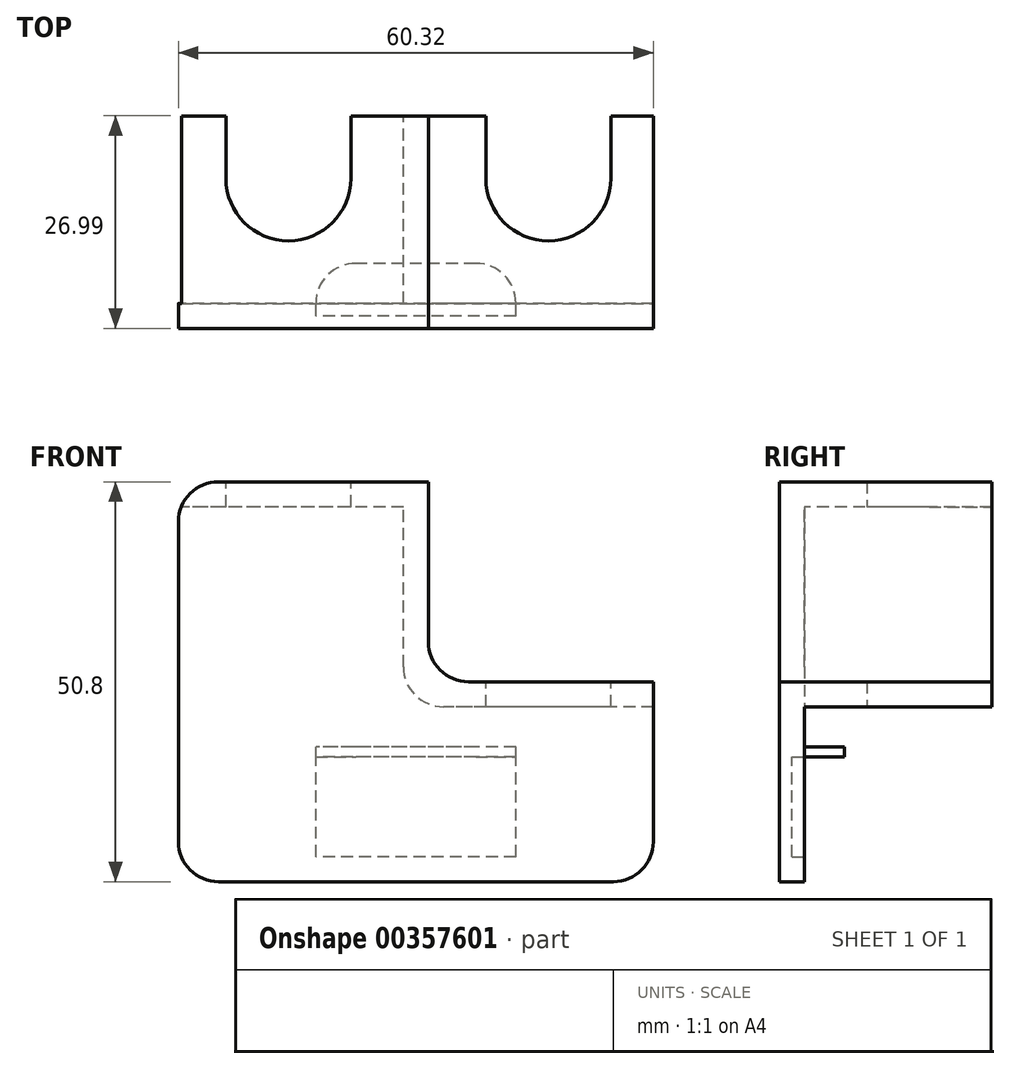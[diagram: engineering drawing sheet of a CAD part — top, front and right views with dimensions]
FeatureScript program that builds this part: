
annotation { "Feature Type Name" : "Feature", "Feature Type Description" : "" }
export const myFeature = defineFeature(function(context is Context, id is Id, definition is map)
    precondition{}
    {
        {
            var Q0;
            Q0=qCreatedBy(makeId("Front.planeOp"),FACE);
            var sketch = newSketch(context, id + "F0", { "sketchPlane" : qUnion([Q0])});
            skLineSegment(sketch, "E0", {"start": v(-28.58, 25.4) * mm, "end": v(0, 25.4) * mm});
            skLineSegment(sketch, "E1", {"start": v(0, 25.4) * mm, "end": v(0, 0) * mm});
            skLineSegment(sketch, "E2", {"start": v(0, 0) * mm, "end": v(25.4, 0) * mm});
            skLineSegment(sketch, "E3", {"start": v(25.4, 0) * mm, "end": v(25.4, -3.18) * mm});
            skLineSegment(sketch, "E4", {"start": v(25.4, -3.18) * mm, "end": v(-3.18, -3.18) * mm});
            skLineSegment(sketch, "E5", {"start": v(-3.18, -3.18) * mm, "end": v(-3.18, 22.22) * mm});
            skLineSegment(sketch, "E6", {"start": v(-3.18, 22.22) * mm, "end": v(-28.58, 22.22) * mm});
            skLineSegment(sketch, "E7", {"start": v(-28.58, 22.22) * mm, "end": v(-28.58, 25.4) * mm});
            skSolve(sketch);
        }
        {
            var Q0;
            Q0=makeQuery(id+"F0.imprint","IMPRINT",FACE,{"disambiguationData":[TD([[makeQuery(id+"F0.imprint","IMPRINT",EDGE,{"derivedFrom":sQuery(id+"F0.wireOp",EDGE,"E0")}),-1.0]])]});
            extrude(context, id + "F1", {"entities" : qUnion([Q0]), "offsetDistance" : 25.4 * mm, "depth" : 28.57 * mm});
        }
        {
            var Q0;
            Q0=makeQuery(id+"F1.opExtrude","SWEPT_FACE",FACE,{"disambiguationData":[OSD([sQuery(id+"F0.wireOp",EDGE,"E4")])]});
            var sketch = newSketch(context, id + "F2", { "sketchPlane" : qUnion([Q0])});
            skCircle(sketch, "E8", {"center": v(-17.78, 12.7) * mm, "radius": 7.94 * mm});
            skCircle(sketch, "E9", {"center": v(15.24, 12.7) * mm, "radius": 7.94 * mm});
            skSolve(sketch);
        }
        {
            var Q0;
            Q0=makeQuery(id+"F2.imprint","IMPRINT",FACE,{"disambiguationData":[TD([[makeQuery(id+"F2.imprint","IMPRINT",EDGE,{"derivedFrom":sQuery(id+"F2.wireOp",EDGE,"E8")}),1.0]])]});
            var Q1;
            Q1=makeQuery(id+"F2.imprint","IMPRINT",FACE,{"disambiguationData":[TD([[makeQuery(id+"F2.imprint","IMPRINT",EDGE,{"derivedFrom":sQuery(id+"F2.wireOp",EDGE,"E9")}),1.0]])]});
            var Q2;
            Q2=makeQuery(id+"F2.imprint","IMPRINT",FACE,{"disambiguationData":[TD([[makeQuery(id+"F2.imprint","IMPRINT",EDGE,{"derivedFrom":sQuery(id+"F2.wireOp",EDGE,"E9")}),1.0]])]});
            extrude(context, id + "F3", {"entities" : qUnion([Q0, Q1, Q2]), "operationType" : NewBodyOperationType.REMOVE, "oppositeDirection" : true, "depth" : 50.8 * mm});
        }
        {
            var Q0;
            Q0=makeQuery(id+"F1.opExtrude","SWEPT_FACE",FACE,{"disambiguationData":[OSD([sQuery(id+"F0.wireOp",EDGE,"E0")])]});
            var sketch = newSketch(context, id + "F4", { "sketchPlane" : qUnion([Q0])});
            skLineSegment(sketch, "E10.bottom", {"start": v(-28.58, 0) * mm, "end": v(25.4, 0) * mm});
            skLineSegment(sketch, "E10.top", {"start": v(-28.58, -28.58) * mm, "end": v(25.4, -28.58) * mm});
            skLineSegment(sketch, "E10.left", {"start": v(-28.58, 0) * mm, "end": v(-28.58, -28.58) * mm});
            skLineSegment(sketch, "E10.right", {"start": v(25.4, 0) * mm, "end": v(25.4, -28.58) * mm});
            skLineSegment(sketch, "E11.0", {"start": v(-31.75, 3.18) * mm, "end": v(28.57, 3.18) * mm});
            skLineSegment(sketch, "E12.0", {"start": v(-31.75, 3.18) * mm, "end": v(-31.75, -31.75) * mm});
            skLineSegment(sketch, "E12.1", {"start": v(-31.75, -31.75) * mm, "end": v(28.57, -31.75) * mm});
            skLineSegment(sketch, "E12.2", {"start": v(28.57, 3.17) * mm, "end": v(28.57, -31.75) * mm});
            skSolve(sketch);
        }
        {
            var Q0;
            {var subQ4=sQuery(id+"F4.wireOp",EDGE,"E10.left");Q0=makeQuery(id+"F4.imprint","IMPRINT",FACE,{"disambiguationData":[TD([[makeQuery(id+"F4.imprint","IMPRINT",EDGE,{"derivedFrom":subQ4}),1.0]])]});}
            extrude(context, id + "F5", {"entities" : qUnion([Q0]), "operationType" : NewBodyOperationType.ADD, "oppositeDirection" : true, "depth" : 50.8 * mm});
        }
        {
            var Q0;
            {var subQ2=sQuery(id+"F4.wireOp",EDGE,"E10.top");Q0=makeQuery(id+"F5.boolean.opBoolean","SPLIT",FACE,{"disambiguationData":[TD([makeQuery(id+"F1.opExtrude","SWEPT_FACE",FACE,{"disambiguationData":[OSD([sQuery(id+"F0.wireOp",EDGE,"E4")])]})])],"derivedFrom":makeQuery(id+"F5.opExtrude","SWEPT_FACE",FACE,{"disambiguationData":[OSD([subQ2])]})});}
            var sketch = newSketch(context, id + "F6", { "sketchPlane" : qUnion([Q0])});
            skLineSegment(sketch, "E13.bottom", {"start": v(-11.11, -22.23) * mm, "end": v(14.29, -22.23) * mm});
            skLineSegment(sketch, "E13.top", {"start": v(-11.11, -9.53) * mm, "end": v(14.29, -9.53) * mm});
            skLineSegment(sketch, "E13.left", {"start": v(-11.11, -22.23) * mm, "end": v(-11.11, -9.53) * mm});
            skLineSegment(sketch, "E13.right", {"start": v(14.29, -22.23) * mm, "end": v(14.29, -9.53) * mm});
            skPoint(sketch, "E13.middle", {"position": v(1.59, -15.88) * mm});
            skSolve(sketch);
        }
        {
            var Q0;
            Q0=makeQuery(id+"F6.imprint","IMPRINT",FACE,{"disambiguationData":[TD([[makeQuery(id+"F6.imprint","IMPRINT",EDGE,{"derivedFrom":sQuery(id+"F6.wireOp",EDGE,"E13.bottom")}),1.0]])]});
            extrude(context, id + "F7", {"entities" : qUnion([Q0]), "operationType" : NewBodyOperationType.REMOVE, "oppositeDirection" : true, "depth" : 1.59 * mm});
        }
        {
            var Q0;
            Q0=makeQuery(id+"F5.boolean.opBoolean","MERGE",FACE,{"derivedFrom":[makeQuery(id+"F1.opExtrude","SWEPT_FACE",FACE,{"disambiguationData":[OSD([sQuery(id+"F0.wireOp",EDGE,"E0")])]}),makeQuery(id+"F5.opExtrude","CAP_FACE",FACE,{"disambiguationData":[OSD([sQuery(id+"F4.wireOp",EDGE,"E10.bottom"),sQuery(id+"F4.wireOp",EDGE,"E10.top"),sQuery(id+"F4.wireOp",EDGE,"E10.left"),sQuery(id+"F4.wireOp",EDGE,"E10.right"),sQuery(id+"F4.wireOp",EDGE,"E11.0"),sQuery(id+"F4.wireOp",EDGE,"E12.0"),sQuery(id+"F4.wireOp",EDGE,"E12.1"),sQuery(id+"F4.wireOp",EDGE,"E12.2")])],"isStart":true})]});
            var sketch = newSketch(context, id + "F8", { "sketchPlane" : qUnion([Q0])});
            skLineSegment(sketch, "E14.bottom", {"start": v(-31.75, -4.76) * mm, "end": v(28.57, -4.76) * mm});
            skLineSegment(sketch, "E14.top", {"start": v(-31.75, 3.18) * mm, "end": v(28.57, 3.18) * mm});
            skLineSegment(sketch, "E14.left", {"start": v(-31.75, -4.76) * mm, "end": v(-31.75, 3.18) * mm});
            skLineSegment(sketch, "E14.right", {"start": v(28.57, -4.76) * mm, "end": v(28.57, 3.18) * mm});
            skLineSegment(sketch, "E15", {"start": v(-25.72, -4.76) * mm, "end": v(-25.72, -12.7) * mm});
            skLineSegment(sketch, "E16", {"start": v(-9.84, -12.7) * mm, "end": v(-9.84, -4.76) * mm});
            skLineSegment(sketch, "E17", {"start": v(7.3, -4.76) * mm, "end": v(7.3, -12.7) * mm});
            skLineSegment(sketch, "E18", {"start": v(23.18, -4.76) * mm, "end": v(23.18, -12.7) * mm});
            skCircle(sketch, "E19", {"center": v(15.24, -12.7) * mm, "radius": 7.94 * mm});
            skSolve(sketch);
        }
        {
            var Q0;
            {var subQ1=sQuery(id+"F4.wireOp",EDGE,"E12.0");var subQ2=sQuery(id+"F4.wireOp",EDGE,"E11.0");var subQ3=makeQuery(id+"Fs04usrGWM9eHkK_1.opFillet","BLEND_EDGE",EDGE,{"blendedFrom":[makeQuery(id+"F5.opExtrude","SWEPT_EDGE",EDGE,{"disambiguationData":[OSD([subQ2,subQ1])]}),makeQuery(id+"F5.boolean.opBoolean","MERGE",FACE,{"derivedFrom":[makeQuery(id+"F1.opExtrude","SWEPT_FACE",FACE,{"disambiguationData":[OSD([sQuery(id+"F0.wireOp",EDGE,"E0")])]}),makeQuery(id+"F5.opExtrude","CAP_FACE",FACE,{"disambiguationData":[OSD([sQuery(id+"F4.wireOp",EDGE,"E10.bottom"),sQuery(id+"F4.wireOp",EDGE,"E10.top"),sQuery(id+"F4.wireOp",EDGE,"E10.left"),sQuery(id+"F4.wireOp",EDGE,"E10.right"),subQ2,subQ1,sQuery(id+"F4.wireOp",EDGE,"E12.1"),sQuery(id+"F4.wireOp",EDGE,"E12.2")])],"isStart":true})]})],"blendedInto":[makeQuery(id+"F5.boolean.opBoolean","MERGE",FACE,{"derivedFrom":[makeQuery(id+"F1.opExtrude","SWEPT_FACE",FACE,{"disambiguationData":[OSD([sQuery(id+"F0.wireOp",EDGE,"E0")])]}),makeQuery(id+"F5.opExtrude","CAP_FACE",FACE,{"disambiguationData":[OSD([sQuery(id+"F4.wireOp",EDGE,"E10.bottom"),sQuery(id+"F4.wireOp",EDGE,"E10.top"),sQuery(id+"F4.wireOp",EDGE,"E10.left"),sQuery(id+"F4.wireOp",EDGE,"E10.right"),subQ2,subQ1,sQuery(id+"F4.wireOp",EDGE,"E12.1"),sQuery(id+"F4.wireOp",EDGE,"E12.2")])],"isStart":true})]})]});Q0=makeQuery(id+"F8.imprint","IMPRINT",FACE,{"disambiguationData":[TD([[makeQuery(id+"F8.imprint","IMPRINT",EDGE,{"derivedFrom":subQ3}),-1.0]])]});}
            var Q1;
            {var subQ1=sQuery(id+"F4.wireOp",EDGE,"E12.2");var subQ2=sQuery(id+"F4.wireOp",EDGE,"E11.0");var subQ3=makeQuery(id+"Fs04usrGWM9eHkK_1.opFillet","BLEND_EDGE",EDGE,{"blendedFrom":[makeQuery(id+"F5.opExtrude","SWEPT_EDGE",EDGE,{"disambiguationData":[OSD([subQ2,subQ1])]}),makeQuery(id+"F5.boolean.opBoolean","MERGE",FACE,{"derivedFrom":[makeQuery(id+"F1.opExtrude","SWEPT_FACE",FACE,{"disambiguationData":[OSD([sQuery(id+"F0.wireOp",EDGE,"E0")])]}),makeQuery(id+"F5.opExtrude","CAP_FACE",FACE,{"disambiguationData":[OSD([sQuery(id+"F4.wireOp",EDGE,"E10.bottom"),sQuery(id+"F4.wireOp",EDGE,"E10.top"),sQuery(id+"F4.wireOp",EDGE,"E10.left"),sQuery(id+"F4.wireOp",EDGE,"E10.right"),subQ2,sQuery(id+"F4.wireOp",EDGE,"E12.0"),sQuery(id+"F4.wireOp",EDGE,"E12.1"),subQ1])],"isStart":true})]})],"blendedInto":[makeQuery(id+"F5.boolean.opBoolean","MERGE",FACE,{"derivedFrom":[makeQuery(id+"F1.opExtrude","SWEPT_FACE",FACE,{"disambiguationData":[OSD([sQuery(id+"F0.wireOp",EDGE,"E0")])]}),makeQuery(id+"F5.opExtrude","CAP_FACE",FACE,{"disambiguationData":[OSD([sQuery(id+"F4.wireOp",EDGE,"E10.bottom"),sQuery(id+"F4.wireOp",EDGE,"E10.top"),sQuery(id+"F4.wireOp",EDGE,"E10.left"),sQuery(id+"F4.wireOp",EDGE,"E10.right"),subQ2,sQuery(id+"F4.wireOp",EDGE,"E12.0"),sQuery(id+"F4.wireOp",EDGE,"E12.1"),subQ1])],"isStart":true})]})]});Q1=makeQuery(id+"F8.imprint","IMPRINT",FACE,{"disambiguationData":[TD([[makeQuery(id+"F8.imprint","IMPRINT",EDGE,{"derivedFrom":subQ3}),-1.0]])]});}
            var Q2;
            {var subQ0=sQuery(id+"F8.wireOp",EDGE,"E17");Q2=makeQuery(id+"F8.imprint","IMPRINT",FACE,{"disambiguationData":[TD([[makeQuery(id+"F8.imprint","IMPRINT",EDGE,{"derivedFrom":subQ0}),1.0]])]});}
            var Q3;
            {var subQ0=sQuery(id+"F8.wireOp",EDGE,"E18");Q3=makeQuery(id+"F8.imprint","IMPRINT",FACE,{"disambiguationData":[TD([[makeQuery(id+"F8.imprint","IMPRINT",EDGE,{"derivedFrom":subQ0}),-1.0]])]});}
            var Q4;
            {var subQ8=makeQuery(id+"F5.opExtrude","CAP_EDGE",EDGE,{"disambiguationData":[OSD([sQuery(id+"F4.wireOp",EDGE,"E10.bottom")])],"isStart":true});Q4=makeQuery(id+"F8.imprint","IMPRINT",FACE,{"disambiguationData":[TD([[makeQuery(id+"F8.imprint","IMPRINT",EDGE,{"derivedFrom":subQ8}),-1.0]])]});}
            var Q5;
            {var subQ5=sQuery(id+"F4.wireOp",EDGE,"E10.bottom");var subQ19=makeQuery(id+"F5.opExtrude","CAP_EDGE",EDGE,{"disambiguationData":[OSD([subQ5])],"isStart":true});Q5=makeQuery(id+"F8.imprint","IMPRINT",FACE,{"disambiguationData":[TD([[makeQuery(id+"F8.imprint","IMPRINT",EDGE,{"derivedFrom":subQ19}),1.0]])]});}
            var Q6;
            {var subQ0=sQuery(id+"F8.wireOp",EDGE,"E16");Q6=makeQuery(id+"F8.imprint","IMPRINT",FACE,{"disambiguationData":[TD([[makeQuery(id+"F8.imprint","IMPRINT",EDGE,{"derivedFrom":subQ0}),1.0]])]});}
            var Q7;
            {var subQ0=sQuery(id+"F8.wireOp",EDGE,"E15");Q7=makeQuery(id+"F8.imprint","IMPRINT",FACE,{"disambiguationData":[TD([[makeQuery(id+"F8.imprint","IMPRINT",EDGE,{"derivedFrom":subQ0}),1.0]])]});}
            extrude(context, id + "F9", {"entities" : qUnion([Q0, Q1, Q2, Q3, Q4, Q5, Q6, Q7]), "operationType" : NewBodyOperationType.REMOVE, "endBound" : BoundingType.THROUGH_ALL, "oppositeDirection" : true, "depth" : 25.4 * mm, "offsetDistance" : 25.4 * mm});
        }
        {
            var Q0;
            Q0=makeQuery(id+"F5.opExtrude","SWEPT_FACE",FACE,{"disambiguationData":[OSD([sQuery(id+"F4.wireOp",EDGE,"E10.left")])]});
            extrude(context, id + "F10", {"entities" : qUnion([Q0]), "operationType" : NewBodyOperationType.REMOVE, "oppositeDirection" : true, "depth" : 25.4 * mm, "offsetDistance" : 25.4 * mm});
        }
        {
            var Q0;
            {var subQ1=sQuery(id+"F4.wireOp",EDGE,"E10.right");Q0=makeQuery(id+"F5.boolean.opBoolean","SPLIT",FACE,{"disambiguationData":[TD([makeQuery(id+"F1.opExtrude","SWEPT_FACE",FACE,{"disambiguationData":[OSD([sQuery(id+"F0.wireOp",EDGE,"E4")])]})])],"derivedFrom":makeQuery(id+"F5.opExtrude","SWEPT_FACE",FACE,{"disambiguationData":[OSD([subQ1])]})});}
            extrude(context, id + "F11", {"entities" : qUnion([Q0]), "operationType" : NewBodyOperationType.REMOVE, "oppositeDirection" : true, "depth" : 25.4 * mm, "offsetDistance" : 25.4 * mm});
        }
        {
            var Q0;
            {var subQ0=sQuery(id+"F4.wireOp",EDGE,"E10.right");Q0=makeQuery(id+"F5.boolean.opBoolean","SPLIT",FACE,{"disambiguationData":[TD([makeQuery(id+"F1.opExtrude","SWEPT_FACE",FACE,{"disambiguationData":[OSD([sQuery(id+"F0.wireOp",EDGE,"E0")])]})])],"derivedFrom":makeQuery(id+"F5.opExtrude","SWEPT_FACE",FACE,{"disambiguationData":[OSD([subQ0])]})});}
            extrude(context, id + "F12", {"entities" : qUnion([Q0]), "operationType" : NewBodyOperationType.REMOVE, "oppositeDirection" : true, "depth" : 25.4 * mm, "offsetDistance" : 25.4 * mm});
        }
        {
            var Q0;
            {var subQ0=sQuery(id+"F4.wireOp",EDGE,"E10.right");var subQ1=sQuery(id+"F4.wireOp",EDGE,"E10.top");Q0=makeQuery(id+"F12.boolean.opBoolean","MERGE",FACE,{"derivedFrom":[makeQuery(id+"F5.boolean.opBoolean","SPLIT",FACE,{"disambiguationData":[TD([makeQuery(id+"F1.opExtrude","SWEPT_FACE",FACE,{"disambiguationData":[OSD([sQuery(id+"F0.wireOp",EDGE,"E0")])]})])],"derivedFrom":makeQuery(id+"F5.opExtrude","SWEPT_FACE",FACE,{"disambiguationData":[OSD([subQ1])]})})],"fromTools":[makeQuery(id+"F12.opExtrude","SWEPT_FACE",FACE,{"disambiguationData":[OSD([subQ1,subQ0])]})]});}
            extrude(context, id + "F13", {"entities" : qUnion([Q0]), "operationType" : NewBodyOperationType.REMOVE, "oppositeDirection" : true, "depth" : 25.4 * mm, "offsetDistance" : 25.4 * mm});
        }
        {
            var Q0;
            {var subQ0=sQuery(id+"F0.wireOp",EDGE,"E2");var subQ1=sQuery(id+"F0.wireOp",EDGE,"E1");Q0=makeQuery(id+"F13.boolean.opBoolean","MERGE",EDGE,{"derivedFrom":[makeQuery(id+"F1.opExtrude","SWEPT_EDGE",EDGE,{"disambiguationData":[OSD([subQ1,subQ0])]})],"fromTools":[makeQuery(id+"F13.opExtrude","SWEPT_EDGE",EDGE,{"disambiguationData":[OSD([subQ1,subQ0])]})]});}
            var Q1;
            {var subQ0=sQuery(id+"F0.wireOp",EDGE,"E1");var subQ1=sQuery(id+"F0.wireOp",EDGE,"E0");Q1=makeQuery(id+"F13.boolean.opBoolean","MERGE",EDGE,{"derivedFrom":[makeQuery(id+"F1.opExtrude","SWEPT_EDGE",EDGE,{"disambiguationData":[OSD([subQ1,subQ0])]})],"fromTools":[makeQuery(id+"F13.opExtrude","SWEPT_EDGE",EDGE,{"disambiguationData":[OSD([subQ1,subQ0])]})]});}
            var Q2;
            {var subQ0=sQuery(id+"F4.wireOp",EDGE,"E12.2");var subQ1=sQuery(id+"F0.wireOp",EDGE,"E3");var subQ2=sQuery(id+"F0.wireOp",EDGE,"E2");Q2=makeQuery(id+"F13.boolean.opBoolean","MERGE",EDGE,{"derivedFrom":[makeQuery(id+"F12.boolean.opBoolean","INTERSECT",EDGE,{"derivedFrom":[makeQuery(id+"F5.opExtrude","SWEPT_FACE",FACE,{"disambiguationData":[OSD([subQ0])]}),makeQuery(id+"F12.opExtrude","SWEPT_FACE",FACE,{"disambiguationData":[OSD([subQ2,subQ1])]})]})],"fromTools":[makeQuery(id+"F13.opExtrude","SWEPT_EDGE",EDGE,{"disambiguationData":[OSD([subQ2,subQ1,sQuery(id+"F4.wireOp",EDGE,"E10.top"),sQuery(id+"F4.wireOp",EDGE,"E10.right"),subQ0])]})]});}
            var Q3;
            Q3=makeQuery(id+"F5.opExtrude","CAP_EDGE",EDGE,{"disambiguationData":[OSD([sQuery(id+"F4.wireOp",EDGE,"E12.0")])],"isStart":true});
            var Q4;
            Q4=makeQuery(id+"F5.opExtrude","CAP_EDGE",EDGE,{"disambiguationData":[OSD([sQuery(id+"F4.wireOp",EDGE,"E12.2")])],"isStart":false});
            var Q5;
            Q5=makeQuery(id+"F5.opExtrude","CAP_EDGE",EDGE,{"disambiguationData":[OSD([sQuery(id+"F4.wireOp",EDGE,"E12.0")])],"isStart":false});
            fillet(context, id + "F14", {"entities" : qUnion([Q0, Q1, Q2, Q3, Q4, Q5]), "radius" : 5.08 * mm, "tangentPropagation" : true, "allowEdgeOverflow" : false});
        }
        {
            var Q0;
            {var subQ0=sQuery(id+"F4.wireOp",EDGE,"E10.right");var subQ1=sQuery(id+"F4.wireOp",EDGE,"E10.top");var subQ2=sQuery(id+"F4.wireOp",EDGE,"E10.left");Q0=makeQuery(id+"F11.boolean.opBoolean","MERGE",FACE,{"derivedFrom":[makeQuery(id+"F10.boolean.opBoolean","MERGE",FACE,{"derivedFrom":[makeQuery(id+"F5.boolean.opBoolean","SPLIT",FACE,{"disambiguationData":[TD([makeQuery(id+"F1.opExtrude","SWEPT_FACE",FACE,{"disambiguationData":[OSD([sQuery(id+"F0.wireOp",EDGE,"E4")])]})])],"derivedFrom":makeQuery(id+"F5.opExtrude","SWEPT_FACE",FACE,{"disambiguationData":[OSD([subQ1])]})})],"fromTools":[makeQuery(id+"F10.opExtrude","SWEPT_FACE",FACE,{"disambiguationData":[OSD([subQ1,subQ2])]})]})],"fromTools":[makeQuery(id+"F11.opExtrude","SWEPT_FACE",FACE,{"disambiguationData":[OSD([subQ1,subQ0])]})]});}
            var sketch = newSketch(context, id + "F15", { "sketchPlane" : qUnion([Q0])});
            skLineSegment(sketch, "E20.bottom", {"start": v(-11.11, -9.53) * mm, "end": v(14.29, -9.53) * mm});
            skLineSegment(sketch, "E20.top", {"start": v(-11.11, -8.26) * mm, "end": v(14.29, -8.26) * mm});
            skLineSegment(sketch, "E20.left", {"start": v(-11.11, -9.53) * mm, "end": v(-11.11, -8.26) * mm});
            skLineSegment(sketch, "E20.right", {"start": v(14.29, -9.53) * mm, "end": v(14.29, -8.26) * mm});
            skSolve(sketch);
        }
        {
            var Q0;
            Q0 = qSketchRegion(id + "F15", true);
            var Q1;
            Q1=makeQuery(id+"F15.imprint","IMPRINT",FACE,{"disambiguationData":[TD([[makeQuery(id+"F15.imprint","IMPRINT",EDGE,{"derivedFrom":sQuery(id+"F15.wireOp",EDGE,"E20.bottom")}),1.0]])]});
            extrude(context, id + "F16", {"entities" : qUnion([Q0, Q1]), "operationType" : NewBodyOperationType.ADD, "depth" : 5.08 * mm, "offsetDistance" : 25.4 * mm});
        }
        {
            var Q0;
            Q0=makeQuery(id+"F16.opExtrude","CAP_EDGE",EDGE,{"disambiguationData":[OSD([sQuery(id+"F15.wireOp",EDGE,"E20.right")])],"isStart":false});
            var Q1;
            Q1=makeQuery(id+"F16.opExtrude","CAP_EDGE",EDGE,{"disambiguationData":[OSD([sQuery(id+"F15.wireOp",EDGE,"E20.left")])],"isStart":false});
            fillet(context, id + "F17", {"entities" : qUnion([Q0, Q1]), "radius" : 5.08 * mm, "tangentPropagation" : true, "allowEdgeOverflow" : false});
        }
        {
            var Q0;
            Q0=makeQuery(id+"F1.opExtrude","SWEPT_EDGE",EDGE,{"disambiguationData":[OSD([sQuery(id+"F0.wireOp",EDGE,"E4"),sQuery(id+"F0.wireOp",EDGE,"E5")])]});
            fillet(context, id + "F18", {"entities" : qUnion([Q0]), "radius" : 5.08 * mm, "tangentPropagation" : true, "allowEdgeOverflow" : false});
        }
    });
